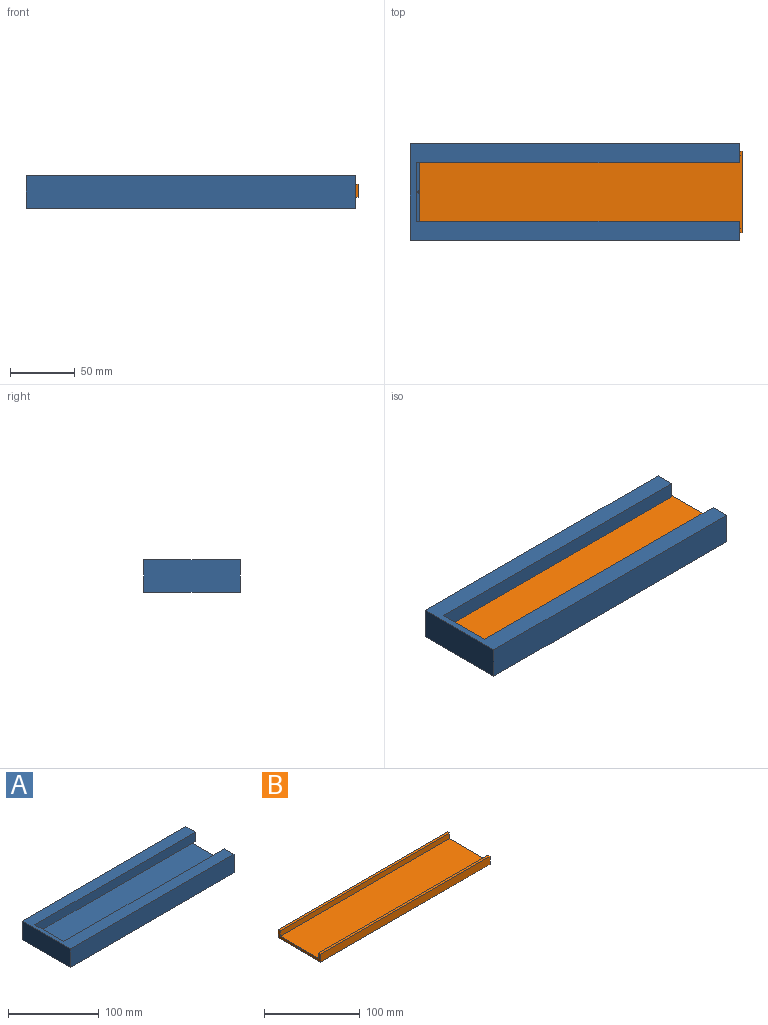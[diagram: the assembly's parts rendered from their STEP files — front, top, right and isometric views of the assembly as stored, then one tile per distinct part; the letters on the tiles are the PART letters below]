
ASSEMBLY  parts=2 mates=1
PART A: 23 faces, bbox 255x75x25 mm
  f0: plane 65x17.5mm, normal (1,0,0), area 948.5mm2, adj f2,f3,f4,f5,f6,f7,f8,f9
  f1: plane 255x25mm, normal (0,1,0), area 6375mm2, adj f13,f15,f16,f17
  f2: plane 250x12.5mm, normal (0,-1,0), area 3125mm2, adj f0,f3,f13,f16
  f3: plane 250x5mm, normal (0,0,-1), area 1250mm2, adj f0,f2,f4,f16
  f4: plane 250x7mm, normal (0,1,0), area 1750mm2, adj f0,f3,f5,f16
  f5: plane 250x5mm, normal (0,0,-1), area 1250mm2, adj f0,f4,f6,f16
  f6: plane 250x12mm, normal (0,-1,0), area 3000mm2, adj f0,f5,f7,f16
  f7: plane 250x65mm, normal (0,0,1), area 16250mm2, adj f0,f6,f8,f16
  f8: plane 250x12mm, normal (0,1,0), area 3000mm2, adj f0,f7,f9,f16
  f9: plane 250x5mm, normal (0,0,-1), area 1250mm2, adj f0,f8,f10,f16
  f10: plane 250x7mm, normal (0,-1,0), area 1750mm2, adj f0,f9,f11,f16
  f11: plane 250x5mm, normal (0,0,-1), area 1250mm2, adj f0,f10,f12,f16
  f12: plane 250x12.5mm, normal (0,1,0), area 3125mm2, adj f0,f11,f13,f16
  f13: plane 255x75mm, normal (0,0,1), area 7875mm2, adj f0,f1,f2,f12,f14,f16,f17
  f14: plane 255x25mm, normal (0,-1,0), area 6375mm2, adj f13,f15,f16,f17
  f15: plane 255x75mm, normal (0,0,-1), area 19125mm2, adj f1,f14,f16,f17
  f16: plane 75x25mm, normal (1,0,0), area 917.5mm2, adj f1,f2,f3,f4,f5,f6,f7,f8
  f17: plane 75x25mm, normal (-1,0,0), area 1875mm2, adj f1,f13,f14,f15
  f18: plane 1x1mm, normal (1,0,0), area 1mm2, adj f19,f20,f21,f22
  f19: cylinder r=1mm len=3mm, axis (0,1,0), area 2.7mm2, adj f0,f18,f20,f21
  f20: cylinder r=1mm len=3mm, axis (0,0,-1), area 2.7mm2, adj f0,f18,f19,f22
  f21: cylinder r=1mm len=3mm, axis (0,0,1), area 2.7mm2, adj f0,f18,f19,f22
  f22: cylinder r=1mm len=3mm, axis (0,-1,0), area 2.7mm2, adj f0,f18,f20,f21
PART B: 15 faces, bbox 251x63x10.2 mm
  f0: plane 63x10.18mm, normal (-1,0,0), area 233.4mm2, adj f1,f2,f3,f4,f5,f6,f7,f8
  f1: plane 250x7mm, normal (0,-1,0), area 1750mm2, adj f0,f2,f8,f9
  f2: plane 250x57mm, normal (0,0,1), area 14250mm2, adj f0,f1,f3,f9
  f3: plane 250x7mm, normal (0,1,0), area 1750mm2, adj f0,f2,f4,f9
  f4: plane 250x3mm, normal (0,0,1), area 750mm2, adj f0,f3,f5,f9
  f5: plane 250x10.18mm, normal (0,-1,0), area 2545.3mm2, adj f0,f4,f6,f9
  f6: plane 250x63mm, normal (0,0,-1), area 15750mm2, adj f0,f5,f7,f9
  f7: plane 250x10.18mm, normal (0,1,0), area 2545.3mm2, adj f0,f6,f8,f9
  f8: plane 250x3mm, normal (0,0,1), area 750mm2, adj f0,f1,f7,f9
  f9: plane 63x10.18mm, normal (1,0,0), area 242.4mm2, adj f1,f2,f3,f4,f5,f6,f7,f8
  f10: plane 1x1mm, normal (-1,0,0), area 1mm2, adj f11,f12,f13,f14
  f11: cylinder r=1mm len=3mm, axis (0,1,0), area 2.7mm2, adj f0,f10,f12,f13
  f12: cylinder r=1mm len=3mm, axis (0,0,-1), area 2.7mm2, adj f0,f10,f11,f14
  f13: cylinder r=1mm len=3mm, axis (0,0,1), area 2.7mm2, adj f0,f10,f11,f14
  f14: cylinder r=1mm len=3mm, axis (0,-1,0), area 2.7mm2, adj f0,f10,f12,f13
PLACE A at identity
PLACE B t=(2,0,0)mm
MATE slider B.f10 <-> A.f18  axis (-1,0,0) through (1,0,-2.5)mm
